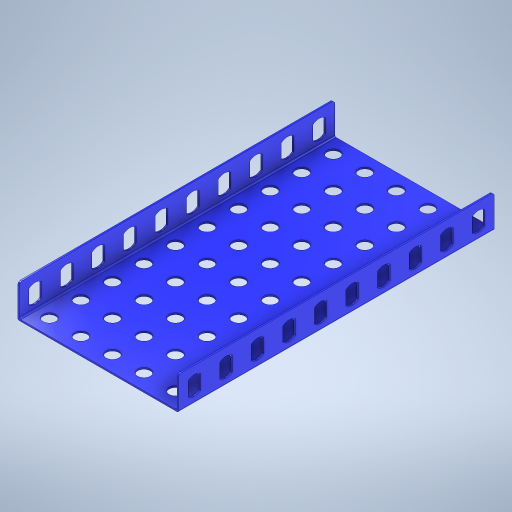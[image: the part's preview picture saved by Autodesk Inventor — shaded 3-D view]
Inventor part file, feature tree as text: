
AUTODESK INVENTOR PART (.ipt)
format: ipt  version: 2024 (Build 280153000, 153)  size: 448,000 bytes
history: native  units: mm
features: extrude x3, sketch x3, other x2, pattern_linear x2, fillet x2
ambient origin geometry x8: Origin, YZ Plane, XZ Plane, XY Plane, X Axis, Y Axis, Z Axis, Center Point
bodies: Body1 (feature_tree)
feature tree (12):
  other  "Těleso1"
  extrude  "Vysunutí1"  Depth=51.0mm
  extrude  "Vysunutí2"  Depth=25.5mm
  pattern_linear  "Obdélníkové pole1"  Spacing1=0.5mm  [1 undecoded]
  other  "Pracovní rovina1"
  extrude  "Vysunutí3"  Depth=0.5mm
  pattern_linear  "Obdélníkové pole2"  Spacing1=0.5mm  [1 undecoded]
  fillet  "Zaoblení1"  Radius=100.0mm
  fillet  "Zaoblení2"  Radius=10.0mm
  sketch  "Náčrt1"
  sketch  "Náčrt2"
  sketch  "Náčrt4"
note: 2 required parameter values undecoded (feature->parameter linkage not recoverable at this tier; creation-order binding heuristic only, values carry confidence <= 0.55)
